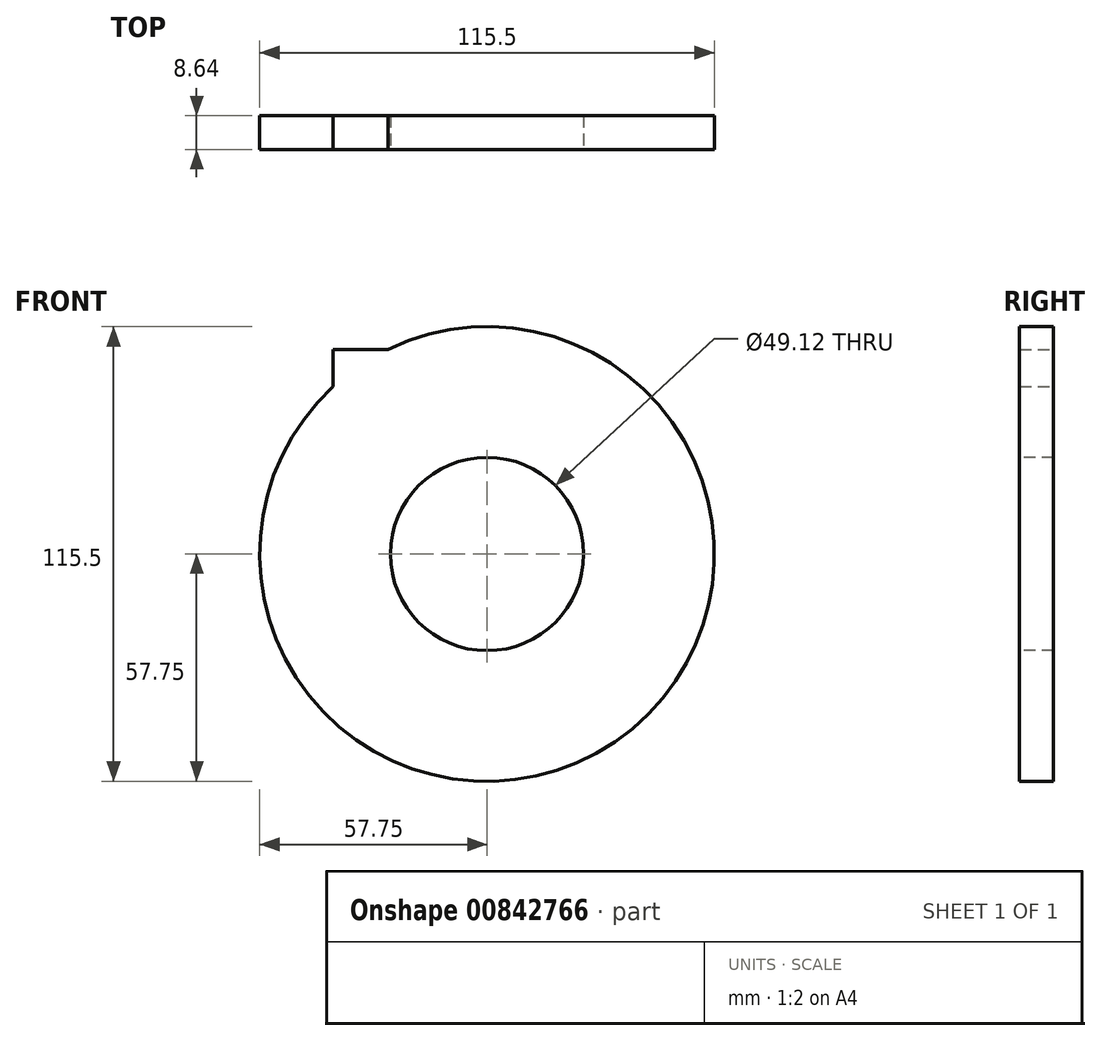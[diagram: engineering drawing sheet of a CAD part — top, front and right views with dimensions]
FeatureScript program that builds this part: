
annotation { "Feature Type Name" : "Feature", "Feature Type Description" : "" }
export const myFeature = defineFeature(function(context is Context, id is Id, definition is map)
    precondition{}
    {
        {
            var Q0;
            Q0=qCreatedBy(makeId("Front.planeOp"),FACE);
            var sketch = newSketch(context, id + "F0", { "sketchPlane" : qUnion([Q0])});
            skCircle(sketch, "E0", {"center": v(0, 0) * mm, "radius": 57.75 * mm});
            skSolve(sketch);
        }
        {
            var Q0;
            Q0=qCreatedBy(makeId("Front.planeOp"),FACE);
            var sketch = newSketch(context, id + "F1", { "sketchPlane" : qUnion([Q0])});
            skLineSegment(sketch, "E1.bottom", {"start": v(-39.1, 26.62) * mm, "end": v(-11.32, 26.62) * mm});
            skLineSegment(sketch, "E1.top", {"start": v(-39.1, 52) * mm, "end": v(-11.32, 52) * mm});
            skLineSegment(sketch, "E1.left", {"start": v(-39.1, 26.62) * mm, "end": v(-39.1, 52) * mm});
            skLineSegment(sketch, "E1.right", {"start": v(-11.32, 26.62) * mm, "end": v(-11.32, 52) * mm});
            skSolve(sketch);
        }
        {
            var Q0;
            Q0=makeQuery(id+"F0.imprint","IMPRINT",FACE,{"disambiguationData":[TD([[makeQuery(id+"F0.imprint","IMPRINT",EDGE,{"derivedFrom":sQuery(id+"F0.wireOp",EDGE,"E0")}),1.0]])]});
            extrude(context, id + "F2", {"entities" : qUnion([Q0]), "depth" : 8.64 * mm, "offsetDistance" : 25.4 * mm});
        }
        {
            var Q0;
            Q0=makeQuery(id+"F1.imprint","IMPRINT",FACE,{"disambiguationData":[TD([[makeQuery(id+"F1.imprint","IMPRINT",EDGE,{"derivedFrom":sQuery(id+"F1.wireOp",EDGE,"E1.bottom")}),1.0]])]});
            extrude(context, id + "F3", {"entities" : qUnion([Q0]), "operationType" : NewBodyOperationType.ADD, "depth" : 8.63 * mm, "offsetDistance" : 25 * mm});
        }
        {
            var Q0;
            Q0=makeQuery(id+"F2.opExtrude","CAP_FACE",FACE,{"disambiguationData":[OSD([sQuery(id+"F0.wireOp",EDGE,"E0")])],"isStart":false});
            var sketch = newSketch(context, id + "F4", { "sketchPlane" : qUnion([Q0])});
            skCircle(sketch, "E2", {"center": v(0, 0) * mm, "radius": 24.56 * mm});
            skSolve(sketch);
        }
        {
            var Q0;
            Q0=makeQuery(id+"F4.imprint","IMPRINT",FACE,{"disambiguationData":[TD([[makeQuery(id+"F4.imprint","IMPRINT",EDGE,{"derivedFrom":sQuery(id+"F4.wireOp",EDGE,"E2")}),1.0]])]});
            extrude(context, id + "F5", {"entities" : qUnion([Q0]), "operationType" : NewBodyOperationType.REMOVE, "oppositeDirection" : true, "depth" : 21.8 * mm, "offsetDistance" : 25 * mm});
        }
    });
